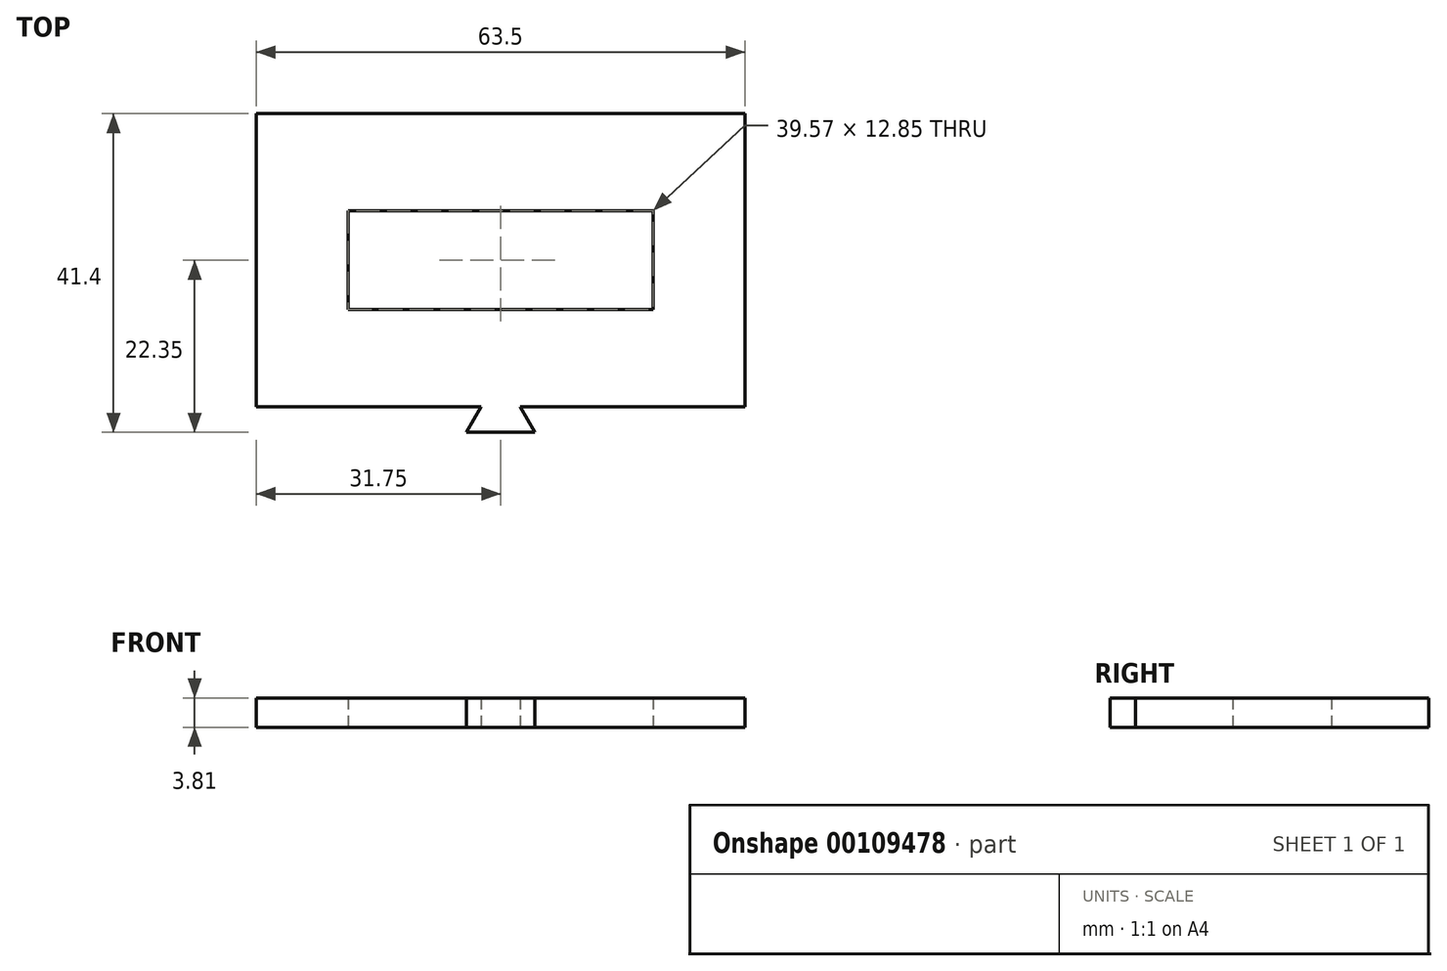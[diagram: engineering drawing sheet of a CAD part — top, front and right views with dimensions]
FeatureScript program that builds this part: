
annotation { "Feature Type Name" : "Feature", "Feature Type Description" : "" }
export const myFeature = defineFeature(function(context is Context, id is Id, definition is map)
    precondition{}
    {
        {
            var Q0;
            Q0=qCreatedBy(makeId("Top.planeOp"),FACE);
            var sketch = newSketch(context, id + "F0", { "sketchPlane" : qUnion([Q0])});
            skLineSegment(sketch, "E0", {"start": v(-5.08, 0) * mm, "end": v(-6.99, -3.3) * mm});
            skLineSegment(sketch, "E1", {"start": v(-6.98, -3.3) * mm, "end": v(1.9, -3.3) * mm});
            skLineSegment(sketch, "E2", {"start": v(1.9, -3.3) * mm, "end": v(0, 0) * mm});
            skLineSegment(sketch, "E3", {"start": v(-5.08, 0) * mm, "end": v(-34.3, 0) * mm});
            skLineSegment(sketch, "E4", {"start": v(0, 0) * mm, "end": v(29.21, 0) * mm});
            skLineSegment(sketch, "E5", {"start": v(-34.3, 0) * mm, "end": v(-34.3, 38.1) * mm});
            skLineSegment(sketch, "E6", {"start": v(29.21, 0) * mm, "end": v(29.21, 38.1) * mm});
            skLineSegment(sketch, "E7", {"start": v(-34.3, 38.1) * mm, "end": v(29.21, 38.1) * mm});
            skLineSegment(sketch, "E8", {"start": v(-2.54, 38.1) * mm, "end": v(-2.54, 25.48) * mm});
            skLineSegment(sketch, "E9", {"start": v(-2.54, 25.48) * mm, "end": v(17.25, 25.48) * mm});
            skLineSegment(sketch, "E10", {"start": v(-2.54, 25.48) * mm, "end": v(-22.33, 25.48) * mm});
            skLineSegment(sketch, "E11", {"start": v(-22.33, 25.48) * mm, "end": v(-22.33, 12.62) * mm});
            skLineSegment(sketch, "E12", {"start": v(-22.33, 12.62) * mm, "end": v(17.25, 12.62) * mm});
            skLineSegment(sketch, "E13", {"start": v(17.25, 12.62) * mm, "end": v(17.25, 25.48) * mm});
            skSolve(sketch);
        }
        {
            var Q0;
            Q0=makeQuery(id+"F0.imprint","IMPRINT",FACE,{"disambiguationData":[TD([[makeQuery(id+"F0.imprint","IMPRINT",EDGE,{"derivedFrom":sQuery(id+"F0.wireOp",EDGE,"E0")}),1.0]])]});
            extrude(context, id + "F1", {"entities" : qUnion([Q0]), "depth" : 3.8 * mm});
        }
    });
